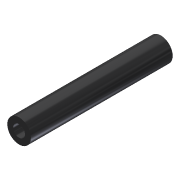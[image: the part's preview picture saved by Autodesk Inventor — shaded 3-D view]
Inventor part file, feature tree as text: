
AUTODESK INVENTOR PART (.ipt)
format: ipt  version: 2013 (Build 170138000, 138)  size: 74,240 bytes
history: native  units: in
note: dims shown in document units (in); Inventor stores cm internally (conversion verified against a paired STEP export)
features: extrude x1, sketch x1
ambient origin geometry x8: Origin, YZ Plane, XZ Plane, XY Plane, X Axis, Y Axis, Z Axis, Center Point
bodies: Solid1 (feature_tree)
feature tree (2):
  extrude  "Extrusion1"  Depth=0.25in
  sketch  "Sketch1"  dims[d0=0.5in d1=0.25in d2=3.0in d3=0.0in]
